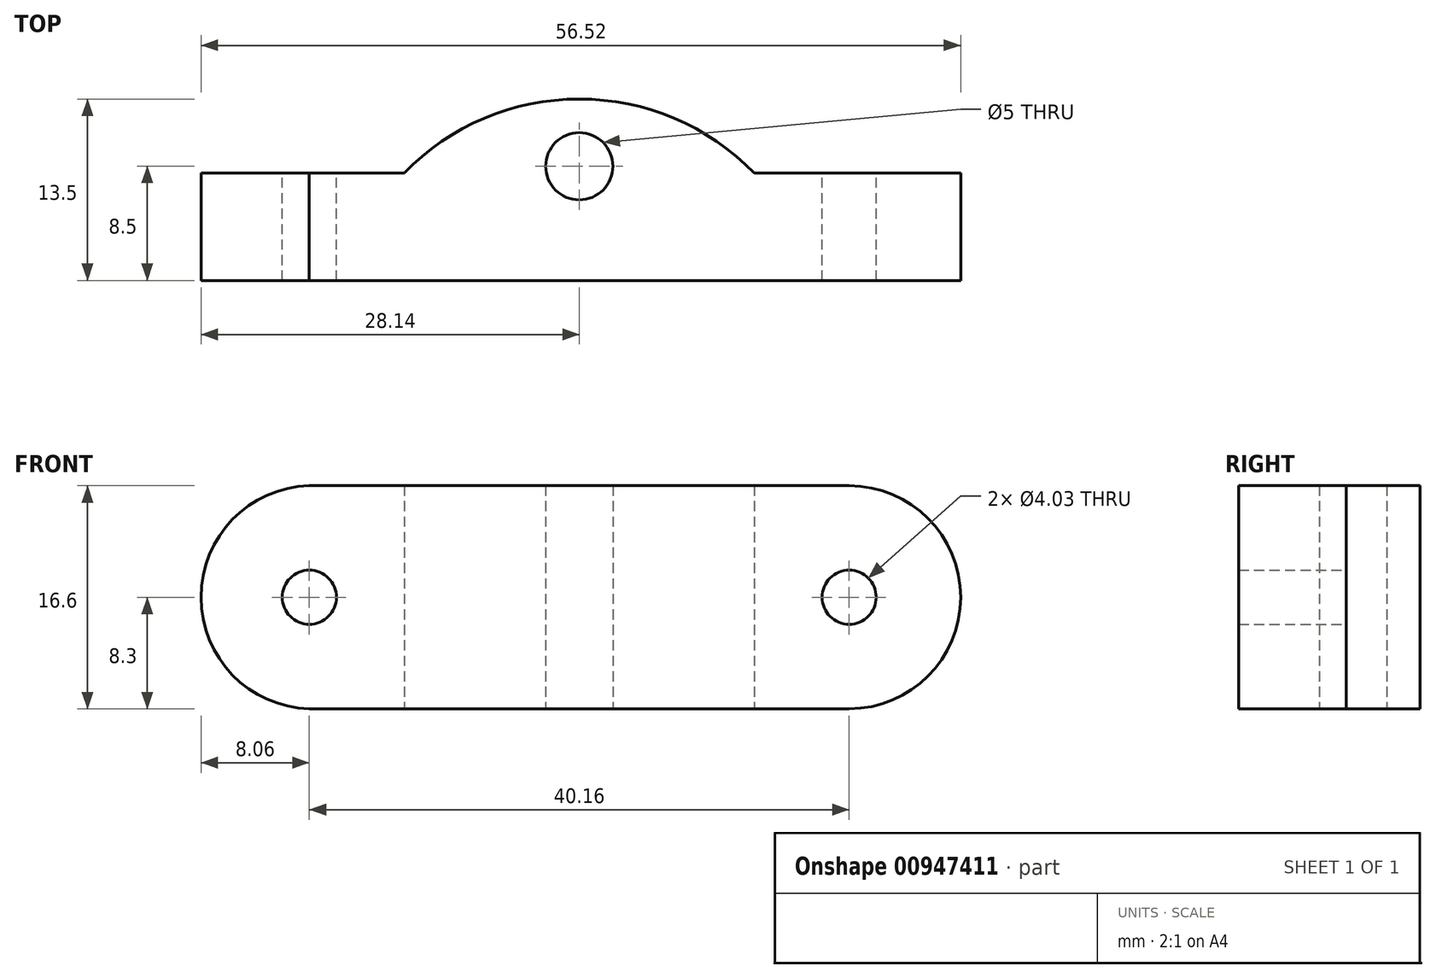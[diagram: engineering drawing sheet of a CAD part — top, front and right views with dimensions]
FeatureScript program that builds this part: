
annotation { "Feature Type Name" : "Feature", "Feature Type Description" : "" }
export const myFeature = defineFeature(function(context is Context, id is Id, definition is map)
    precondition{}
    {
        {
            var Q0;
            Q0=qCreatedBy(makeId("Front.planeOp"),FACE);
            var sketch = newSketch(context, id + "F0", { "sketchPlane" : qUnion([Q0])});
            skLineSegment(sketch, "E0", {"start": v(-20.08, 8.3) * mm, "end": v(20.08, 8.3) * mm});
            skLineSegment(sketch, "E1", {"start": v(-20.08, -8.3) * mm, "end": v(20.08, -8.3) * mm});
            skPoint(sketch, "E2", {"position": v(-20.08, 0) * mm});
            skPoint(sketch, "E3", {"position": v(20.08, 0) * mm});
            skArc(sketch, "E4", {"start": v(-20.08, 8.3) * mm, "mid": v(-28.14, 0) * mm, "end": v(-20.08, -8.3) * mm});
            skArc(sketch, "E5", {"start": v(20.08, -8.3) * mm, "mid": v(28.38, 0) * mm, "end": v(20.08, 8.3) * mm});
            skCircle(sketch, "E6", {"center": v(20.08, 0) * mm, "radius": 2.02 * mm});
            skLineSegment(sketch, "E7", {"start": v(-28.14, 0) * mm, "end": v(28.38, 0) * mm});
            skCircle(sketch, "E8.MirrorC", {"center": v(-20.08, 0) * mm, "radius": 2.02 * mm});
            skSolve(sketch);
        }
        {
            var Q0;
            Q0=qSketchRegion(id+"F0",true);
            extrude(context, id + "F1", {"entities" : qUnion([Q0]), "depth" : 8 * mm, "offsetDistance" : 25 * mm});
        }
        {
            var Q0;
            Q0=qCreatedBy(makeId("Top.planeOp"),FACE);
            var sketch = newSketch(context, id + "F2", { "sketchPlane" : qUnion([Q0])});
            skLineSegment(sketch, "E9", {"start": v(-13.03, 0) * mm, "end": v(-2.45, 0) * mm, "construction": true});
            skArc(sketch, "E10", {"start": v(13.03, 0) * mm, "mid": v(0, 5.5) * mm, "end": v(-13.03, 0) * mm});
            skCircle(sketch, "E11", {"center": v(0, 0.5) * mm, "radius": 2.5 * mm});
            skLineSegment(sketch, "E12", {"start": v(-13.03, 0) * mm, "end": v(-2.45, 0) * mm});
            skLineSegment(sketch, "E13", {"start": v(0, -2) * mm, "end": v(0, -8) * mm, "construction": true});
            skLineSegment(sketch, "E14.trimOffspring", {"start": v(2.45, 0) * mm, "end": v(13.03, 0) * mm, "construction": true});
            skLineSegment(sketch, "E15.trimOffspring", {"start": v(2.45, 0) * mm, "end": v(13.03, 0) * mm});
            skSolve(sketch);
        }
        {
            var Q0;
            Q0=makeQuery(id+"F2.imprint","IMPRINT",FACE,{"disambiguationData":[TD([[makeQuery(id+"F2.imprint","IMPRINT",EDGE,{"derivedFrom":sQuery(id+"F2.wireOp",EDGE,"E10")}),1.0]])]});
            var Q1;
            Q1=makeQuery(id+"F1.opExtrude","SWEPT_FACE",FACE,{"disambiguationData":[OSD([sQuery(id+"F0.wireOp",EDGE,"E0")])]});
            var Q2;
            Q2=makeQuery(id+"F1.opExtrude","SWEPT_FACE",FACE,{"disambiguationData":[OSD([sQuery(id+"F0.wireOp",EDGE,"E1")])]});
            extrude(context, id + "F3", {"entities" : qUnion([Q0]), "operationType" : NewBodyOperationType.ADD, "endBound" : BoundingType.UP_TO_SURFACE, "depth" : 25 * mm, "endBoundEntityFace" : qUnion([Q1]), "offsetDistance" : 25 * mm, "hasSecondDirection" : true, "secondDirectionBound" : SecondDirectionBoundingType.UP_TO_SURFACE, "secondDirectionOppositeDirection" : true, "secondDirectionDepth" : 25 * mm, "secondDirectionBoundEntityFace" : qUnion([Q2])});
        }
        {
            var Q0;
            Q0=qCreatedBy(makeId("Top.planeOp"),FACE);
            var sketch = newSketch(context, id + "F4", { "sketchPlane" : qUnion([Q0])});
            skLineSegment(sketch, "E16", {"start": v(0, 0) * mm, "end": v(0, 0.5) * mm, "construction": true});
            skCircle(sketch, "E17", {"center": v(0, 0.5) * mm, "radius": 2.5 * mm});
            skSolve(sketch);
        }
        {
            var Q0;
            Q0 = qSketchRegion(id + "F4", true);
            extrude(context, id + "F5", {"entities" : qUnion([Q0]), "operationType" : NewBodyOperationType.REMOVE, "endBound" : BoundingType.SYMMETRIC, "oppositeDirection" : true, "depth" : 25 * mm, "offsetDistance" : 25 * mm});
        }
    });
